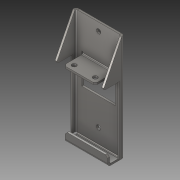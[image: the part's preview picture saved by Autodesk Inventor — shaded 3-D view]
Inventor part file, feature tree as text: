
AUTODESK INVENTOR PART (.ipt)
format: ipt  version: 2018 (Build 220112000, 112)  size: 133,632 bytes
history: native  units: in
note: dims shown in document units (in); Inventor stores cm internally (conversion verified against a paired STEP export)
features: chamfer x1
ambient origin geometry x8: Origin, YZ Plane, XZ Plane, XY Plane, X Axis, Y Axis, Z Axis, Center Point
bodies: Solid1 (feature_tree)
feature tree (1):
  chamfer  "Chamfer8"  [1 undecoded]
note: 1 required parameter value undecoded (feature->parameter linkage not recoverable at this tier; creation-order binding heuristic only, values carry confidence <= 0.55)
